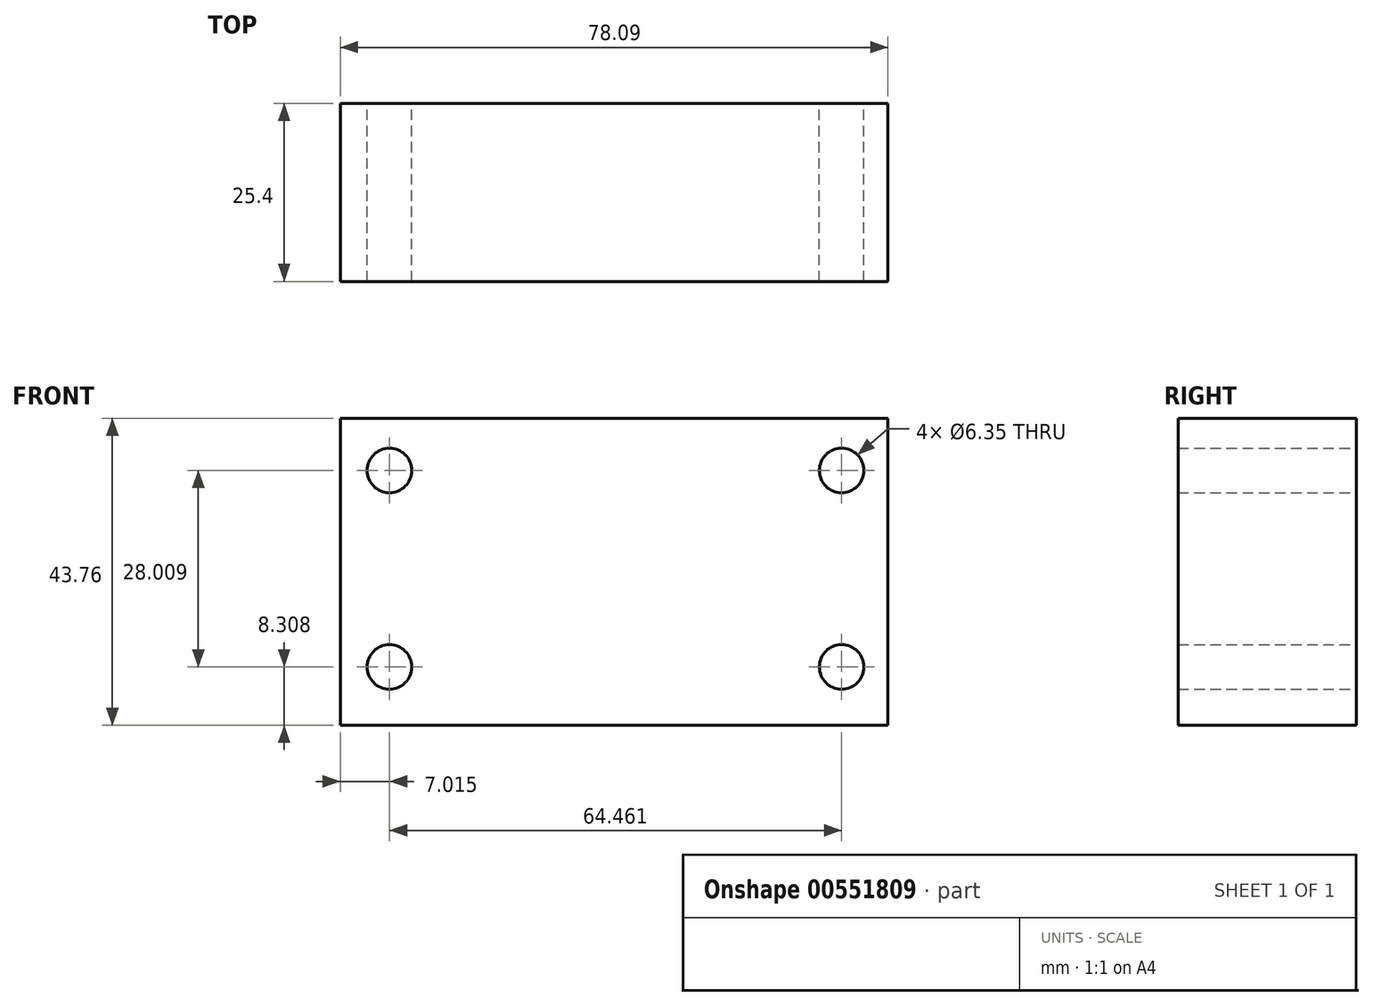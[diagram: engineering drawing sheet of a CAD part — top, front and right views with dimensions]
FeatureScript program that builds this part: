
annotation { "Feature Type Name" : "Feature", "Feature Type Description" : "" }
export const myFeature = defineFeature(function(context is Context, id is Id, definition is map)
    precondition{}
    {
        {
            var Q0;
            Q0=qCreatedBy(makeId("Front.planeOp"),FACE);
            var sketch = newSketch(context, id + "F0", { "sketchPlane" : qUnion([Q0])});
            skLineSegment(sketch, "E0.bottom", {"start": v(-62.62, 56.15) * mm, "end": v(15.47, 56.15) * mm});
            skLineSegment(sketch, "E0.top", {"start": v(-62.62, 12.39) * mm, "end": v(15.47, 12.39) * mm});
            skLineSegment(sketch, "E0.left", {"start": v(-62.62, 56.15) * mm, "end": v(-62.62, 12.39) * mm});
            skLineSegment(sketch, "E0.right", {"start": v(15.47, 56.15) * mm, "end": v(15.47, 12.39) * mm});
            skSolve(sketch);
        }
        {
            var Q0;
            Q0 = qSketchRegion(id + "F0", true);
            extrude(context, id + "F1", {"entities" : qUnion([Q0]), "depth" : 25.4 * mm, "offsetDistance" : 25.4 * mm});
        }
        {
            var Q0;
            Q0=qCreatedBy(makeId("Front.planeOp"),FACE);
            var sketch = newSketch(context, id + "F2", { "sketchPlane" : qUnion([Q0])});
            skLineSegment(sketch, "E1.bottom", {"start": v(-55.6, 48.7) * mm, "end": v(8.86, 48.7) * mm});
            skLineSegment(sketch, "E1.top", {"start": v(-55.6, 20.7) * mm, "end": v(8.86, 20.7) * mm});
            skLineSegment(sketch, "E1.left", {"start": v(-55.6, 48.7) * mm, "end": v(-55.6, 20.7) * mm});
            skLineSegment(sketch, "E1.right", {"start": v(8.86, 48.7) * mm, "end": v(8.86, 20.7) * mm});
            skSolve(sketch);
        }
        {
            var Q0;
            Q0=sQuery(id+"F2.wireOp",VERTEX,"E1.left.start");
            var Q1;
            Q1=sQuery(id+"F2.wireOp",VERTEX,"E1.right.start");
            var Q2;
            Q2=sQuery(id+"F2.wireOp",VERTEX,"E1.top.end");
            var Q3;
            Q3=sQuery(id+"F2.wireOp",VERTEX,"E1.left.end");
            var Q4;
            Q4=makeQuery(id+"F1.opExtrude","SWEPT_BODY",BODY,{"disambiguationData":[OSD([sQuery(id+"F0.wireOp",EDGE,"E0.bottom"),sQuery(id+"F0.wireOp",EDGE,"E0.top"),sQuery(id+"F0.wireOp",EDGE,"E0.left"),sQuery(id+"F0.wireOp",EDGE,"E0.right")])]});
            hole(context, id + "F3", {"style" : HoleStyle.SIMPLE, "endStyle" : HoleEndStyle.THROUGH, "oppositeDirection" : true, "holeDiameter" : 6.35 * mm, "isTappedThrough" : true, "tappedDepth" : 12.7 * mm, "tapClearance" : 3, "locations" : qUnion([Q0, Q1, Q2, Q3]), "scope" : qUnion([Q4])});
        }
    });
